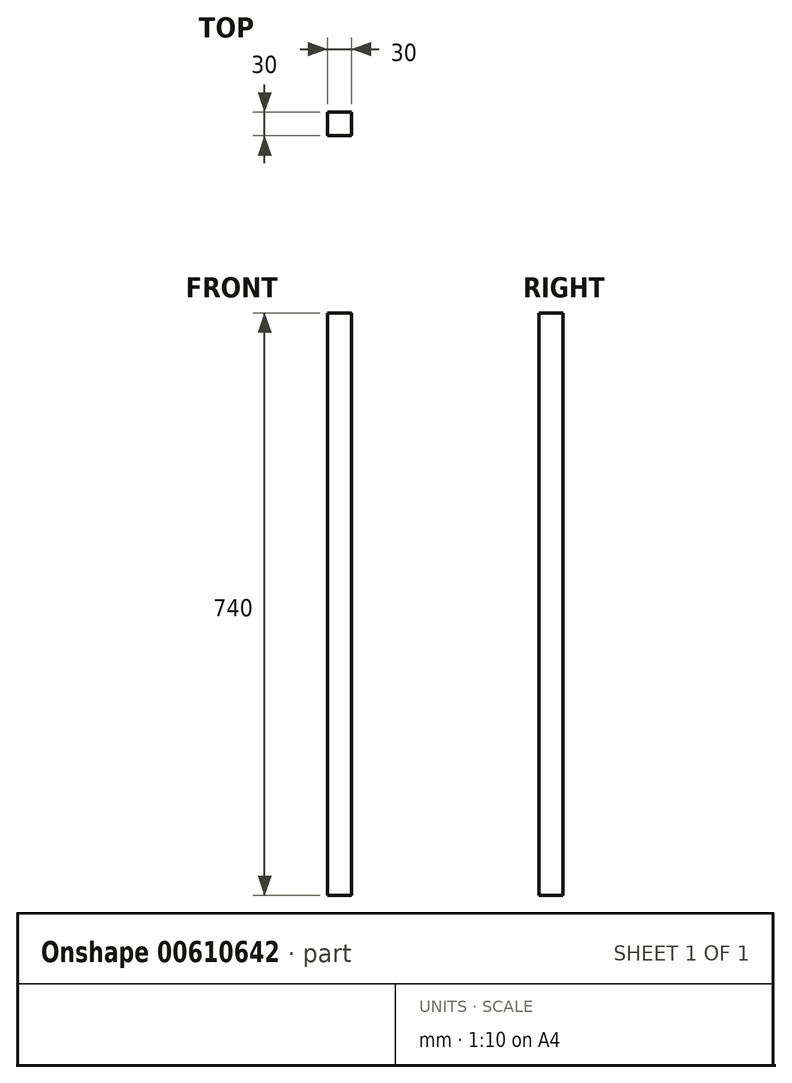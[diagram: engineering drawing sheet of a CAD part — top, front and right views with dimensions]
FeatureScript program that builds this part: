
annotation { "Feature Type Name" : "Feature", "Feature Type Description" : "" }
export const myFeature = defineFeature(function(context is Context, id is Id, definition is map)
    precondition{}
    {
        {
            var Q0;
            Q0=qCreatedBy(makeId("Front.planeOp"),FACE);
            var sketch = newSketch(context, id + "F0", { "sketchPlane" : qUnion([Q0])});
            skLineSegment(sketch, "E0.bottom", {"start": v(-59.04, 521.55) * mm, "end": v(-29.04, 521.55) * mm});
            skLineSegment(sketch, "E0.top", {"start": v(-59.04, -218.45) * mm, "end": v(-29.04, -218.45) * mm});
            skLineSegment(sketch, "E0.left", {"start": v(-59.04, 521.55) * mm, "end": v(-59.04, -218.45) * mm});
            skLineSegment(sketch, "E0.right", {"start": v(-29.04, 521.55) * mm, "end": v(-29.04, -218.45) * mm});
            skSolve(sketch);
        }
        {
            var Q0;
            Q0=qSketchRegion(id+"F0",true);
            extrude(context, id + "F1", {"entities" : qUnion([Q0]), "depth" : 30 * mm});
        }
    });
